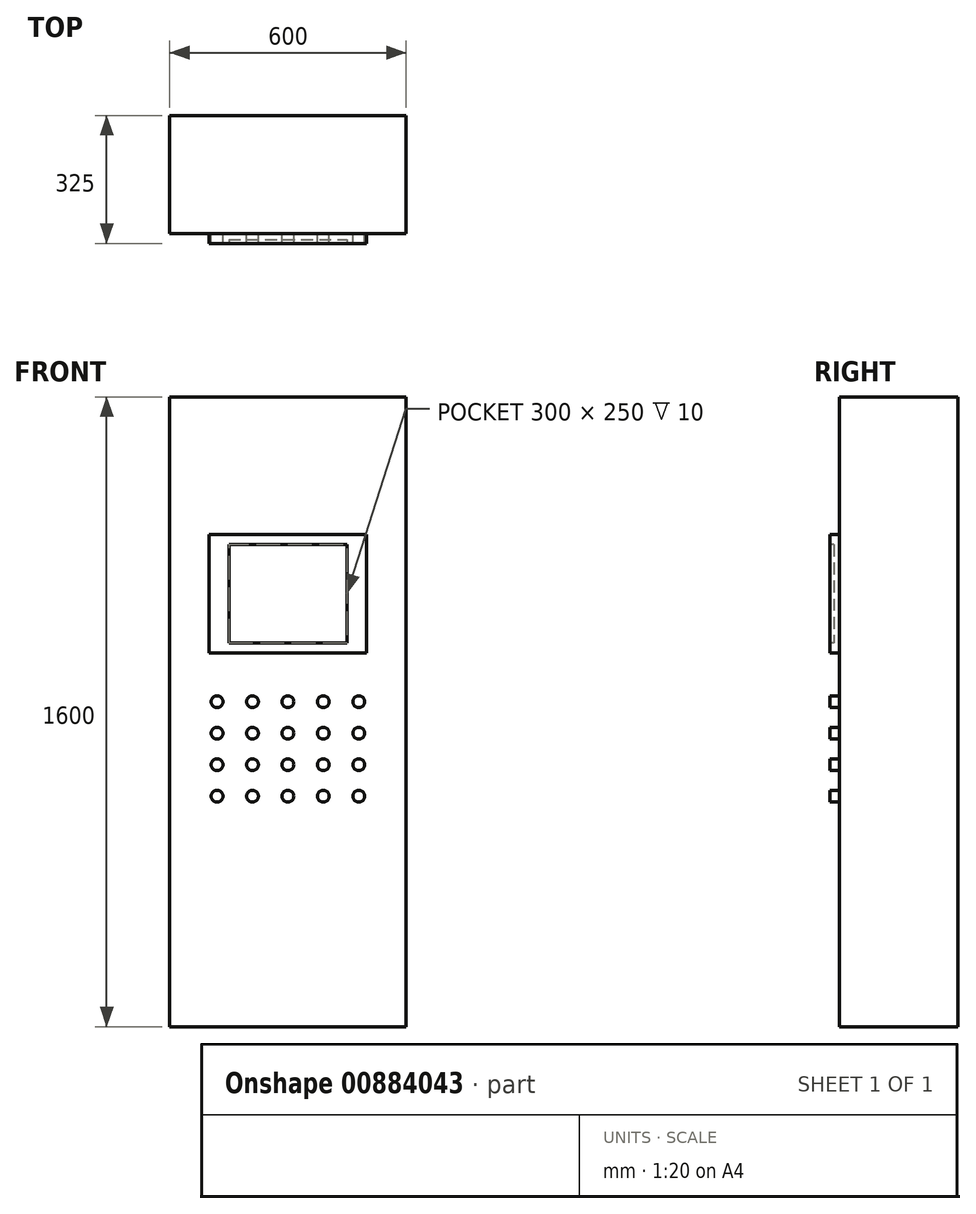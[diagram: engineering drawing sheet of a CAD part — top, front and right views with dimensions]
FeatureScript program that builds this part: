
annotation { "Feature Type Name" : "Feature", "Feature Type Description" : "" }
export const myFeature = defineFeature(function(context is Context, id is Id, definition is map)
    precondition{}
    {
        {
            var Q0;
            Q0=qCreatedBy(makeId("Front.planeOp"),FACE);
            var sketch = newSketch(context, id + "F0", { "sketchPlane" : qUnion([Q0])});
            skLineSegment(sketch, "E0.bottom", {"start": v(0, 0) * mm, "end": v(600, 0) * mm});
            skLineSegment(sketch, "E0.top", {"start": v(0, 1600) * mm, "end": v(600, 1600) * mm});
            skLineSegment(sketch, "E0.left", {"start": v(0, 0) * mm, "end": v(0, 1600) * mm});
            skLineSegment(sketch, "E0.right", {"start": v(600, 0) * mm, "end": v(600, 1600) * mm});
            skSolve(sketch);
        }
        {
            var Q0;
            Q0=makeQuery(id+"F0.imprint","IMPRINT",FACE,{"disambiguationData":[TD([[makeQuery(id+"F0.imprint","IMPRINT",EDGE,{"derivedFrom":sQuery(id+"F0.wireOp",EDGE,"E0.bottom")}),1.0]])]});
            extrude(context, id + "F1", {"entities" : qUnion([Q0]), "depth" : 300 * mm, "offsetDistance" : 25 * mm});
        }
        {
            var Q0;
            Q0=makeQuery(id+"F1.opExtrude","CAP_FACE",FACE,{"disambiguationData":[OSD([sQuery(id+"F0.wireOp",EDGE,"E0.bottom"),sQuery(id+"F0.wireOp",EDGE,"E0.top"),sQuery(id+"F0.wireOp",EDGE,"E0.left"),sQuery(id+"F0.wireOp",EDGE,"E0.right")])],"isStart":false});
            var sketch = newSketch(context, id + "F2", { "sketchPlane" : qUnion([Q0])});
            skLineSegment(sketch, "E1.bottom", {"start": v(100, 1250) * mm, "end": v(500, 1250) * mm});
            skLineSegment(sketch, "E1.top", {"start": v(100, 950) * mm, "end": v(500, 950) * mm});
            skLineSegment(sketch, "E1.left", {"start": v(100, 1250) * mm, "end": v(100, 950) * mm});
            skLineSegment(sketch, "E1.right", {"start": v(500, 1250) * mm, "end": v(500, 950) * mm});
            skSolve(sketch);
        }
        {
            var Q0;
            Q0=makeQuery(id+"F2.imprint","IMPRINT",FACE,{"disambiguationData":[TD([[makeQuery(id+"F2.imprint","IMPRINT",EDGE,{"derivedFrom":sQuery(id+"F2.wireOp",EDGE,"E1.bottom")}),-1.0]])]});
            extrude(context, id + "F3", {"entities" : qUnion([Q0]), "operationType" : NewBodyOperationType.ADD, "depth" : 25 * mm, "offsetDistance" : 25 * mm});
        }
        {
            var Q0;
            Q0=makeQuery(id+"F3.opExtrude","CAP_FACE",FACE,{"disambiguationData":[OSD([sQuery(id+"F2.wireOp",EDGE,"E1.bottom"),sQuery(id+"F2.wireOp",EDGE,"E1.top"),sQuery(id+"F2.wireOp",EDGE,"E1.left"),sQuery(id+"F2.wireOp",EDGE,"E1.right")])],"isStart":false});
            var sketch = newSketch(context, id + "F4", { "sketchPlane" : qUnion([Q0])});
            skLineSegment(sketch, "E2.bottom", {"start": v(150, 1225) * mm, "end": v(450, 1225) * mm});
            skLineSegment(sketch, "E2.top", {"start": v(150, 975) * mm, "end": v(450, 975) * mm});
            skLineSegment(sketch, "E2.left", {"start": v(150, 1225) * mm, "end": v(150, 975) * mm});
            skLineSegment(sketch, "E2.right", {"start": v(450, 1225) * mm, "end": v(450, 975) * mm});
            skSolve(sketch);
        }
        {
            var Q0;
            Q0=makeQuery(id+"F4.imprint","IMPRINT",FACE,{"disambiguationData":[TD([[makeQuery(id+"F4.imprint","IMPRINT",EDGE,{"derivedFrom":sQuery(id+"F4.wireOp",EDGE,"E2.bottom")}),-1.0]])]});
            extrude(context, id + "F5", {"entities" : qUnion([Q0]), "operationType" : NewBodyOperationType.REMOVE, "oppositeDirection" : true, "depth" : 10 * mm, "offsetDistance" : 25 * mm});
        }
        {
            var Q0;
            Q0=makeQuery(id+"F1.opExtrude","CAP_FACE",FACE,{"disambiguationData":[OSD([sQuery(id+"F0.wireOp",EDGE,"E0.bottom"),sQuery(id+"F0.wireOp",EDGE,"E0.top"),sQuery(id+"F0.wireOp",EDGE,"E0.left"),sQuery(id+"F0.wireOp",EDGE,"E0.right")])],"isStart":false});
            var sketch = newSketch(context, id + "F6", { "sketchPlane" : qUnion([Q0])});
            skCircle(sketch, "E3", {"center": v(120, 825.67) * mm, "radius": 15 * mm});
            skCircle(sketch, "E4.0.1.0", {"center": v(120, 745.67) * mm, "radius": 15 * mm});
            skCircle(sketch, "E4.0.2.0", {"center": v(120, 665.67) * mm, "radius": 15 * mm});
            skCircle(sketch, "E4.0.3.0", {"center": v(120, 585.67) * mm, "radius": 15 * mm});
            skCircle(sketch, "E4.1.0.0", {"center": v(210, 825.67) * mm, "radius": 15 * mm});
            skCircle(sketch, "E4.1.1.0", {"center": v(210, 745.67) * mm, "radius": 15 * mm});
            skCircle(sketch, "E4.1.2.0", {"center": v(210, 665.67) * mm, "radius": 15 * mm});
            skCircle(sketch, "E4.1.3.0", {"center": v(210, 585.67) * mm, "radius": 15 * mm});
            skCircle(sketch, "E4.2.0.0", {"center": v(300, 825.67) * mm, "radius": 15 * mm});
            skCircle(sketch, "E4.2.1.0", {"center": v(300, 745.67) * mm, "radius": 15 * mm});
            skCircle(sketch, "E4.2.2.0", {"center": v(300, 665.67) * mm, "radius": 15 * mm});
            skCircle(sketch, "E4.2.3.0", {"center": v(300, 585.67) * mm, "radius": 15 * mm});
            skCircle(sketch, "E4.3.0.0", {"center": v(390, 825.67) * mm, "radius": 15 * mm});
            skCircle(sketch, "E4.3.1.0", {"center": v(390, 745.67) * mm, "radius": 15 * mm});
            skCircle(sketch, "E4.3.2.0", {"center": v(390, 665.67) * mm, "radius": 15 * mm});
            skCircle(sketch, "E4.3.3.0", {"center": v(390, 585.67) * mm, "radius": 15 * mm});
            skCircle(sketch, "E4.4.0.0", {"center": v(480, 825.67) * mm, "radius": 15 * mm});
            skCircle(sketch, "E4.4.1.0", {"center": v(480, 745.67) * mm, "radius": 15 * mm});
            skCircle(sketch, "E4.4.2.0", {"center": v(480, 665.67) * mm, "radius": 15 * mm});
            skCircle(sketch, "E4.4.3.0", {"center": v(480, 585.67) * mm, "radius": 15 * mm});
            skLineSegment(sketch, "E4.direction1", {"start": v(120, 825.67) * mm, "end": v(210, 825.67) * mm, "construction": true});
            skLineSegment(sketch, "E4.direction2", {"start": v(120, 825.67) * mm, "end": v(120, 745.67) * mm, "construction": true});
            skSolve(sketch);
        }
        {
            var Q0;
            Q0=qSketchRegion(id+"F6",true);
            extrude(context, id + "F7", {"entities" : qUnion([Q0]), "depth" : 25 * mm, "offsetDistance" : 25 * mm});
        }
    });
